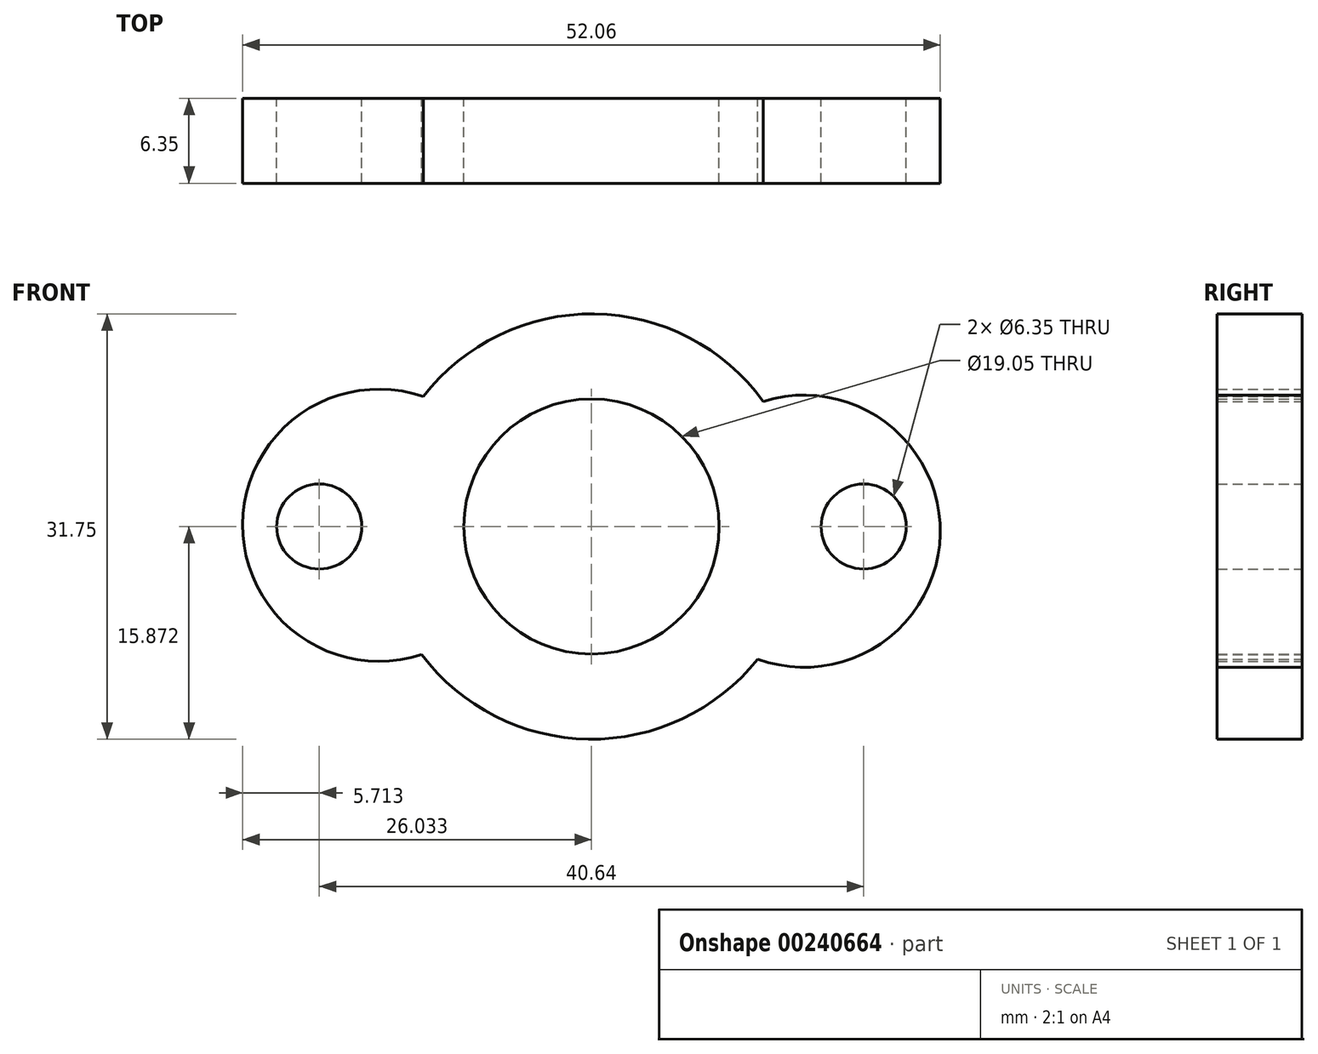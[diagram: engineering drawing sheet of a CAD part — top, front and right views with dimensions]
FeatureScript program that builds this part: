
annotation { "Feature Type Name" : "Feature", "Feature Type Description" : "" }
export const myFeature = defineFeature(function(context is Context, id is Id, definition is map)
    precondition{}
    {
        {
            var Q0;
            Q0=qCreatedBy(makeId("Front.planeOp"),FACE);
            var sketch = newSketch(context, id + "F0", { "sketchPlane" : qUnion([Q0])});
            skCircle(sketch, "E0", {"center": v(-58.59, -37.7) * mm, "radius": 3.18 * mm});
            skCircle(sketch, "E1.0", {"center": v(-58.59, -37.7) * mm, "radius": 9.53 * mm});
            skCircle(sketch, "E2.0", {"center": v(-58.59, -37.7) * mm, "radius": 15.88 * mm});
            skArc(sketch, "E3", {"start": v(-46.18, -47.6) * mm, "mid": v(-32.56, -38.28) * mm, "end": v(-45.76, -28.36) * mm});
            skArc(sketch, "E4", {"start": v(-71.15, -28) * mm, "mid": v(-84.62, -37.55) * mm, "end": v(-71.27, -47.26) * mm});
            skLineSegment(sketch, "E5", {"start": v(-58.59, -37.7) * mm, "end": v(-78.9, -37.7) * mm});
            skLineSegment(sketch, "E6", {"start": v(-58.59, -37.7) * mm, "end": v(-38.27, -37.7) * mm});
            skCircle(sketch, "E7", {"center": v(-38.27, -37.7) * mm, "radius": 3.18 * mm});
            skCircle(sketch, "E8", {"center": v(-78.9, -37.7) * mm, "radius": 3.18 * mm});
            skCircle(sketch, "E9", {"center": v(31.02, -26.4) * mm, "radius": 6.35 * mm});
            skCircle(sketch, "E10.0", {"center": v(31.02, -26.4) * mm, "radius": 12.7 * mm});
            skCircle(sketch, "E11.0", {"center": v(31.02, -26.4) * mm, "radius": 19.05 * mm});
            skArc(sketch, "E12", {"start": v(45.93, -38.26) * mm, "mid": v(62.77, -26.15) * mm, "end": v(45.74, -14.31) * mm});
            skArc(sketch, "E13", {"start": v(16.3, -14.31) * mm, "mid": v(-0.73, -26.15) * mm, "end": v(16.11, -38.26) * mm});
            skPoint(sketch, "E14.endSnap0", {"position": v(-0.73, -26.15) * mm});
            skPoint(sketch, "E15.trimOffspring.end.orphan", {"position": v(62.77, -26.15) * mm});
            skSolve(sketch);
        }
        {
            var Q0;
            {var subQ0=sQuery(id+"F0.wireOp",EDGE,"E4");Q0=makeQuery(id+"F0.imprint","IMPRINT",FACE,{"disambiguationData":[TD([[makeQuery(id+"F0.imprint","IMPRINT",EDGE,{"derivedFrom":subQ0}),1.0]])]});}
            var Q1;
            {var subQ2=sQuery(id+"F0.wireOp",EDGE,"E5");var subQ6=sQuery(id+"F0.wireOp",EDGE,"E1.0");var subQ9=makeQuery(id+"F0.imprint","INTERSECT",VERTEX,{"derivedFrom":[subQ6,subQ2]});Q1=makeQuery(id+"F0.imprint","IMPRINT",FACE,{"disambiguationData":[TD([[makeQuery(id+"F0.imprint","IMPRINT",EDGE,{"disambiguationData":[TD([[subQ9,1.0]])],"derivedFrom":subQ6}),-1.0]])]});}
            var Q2;
            {var subQ5=sQuery(id+"F0.wireOp",EDGE,"E5");var subQ7=sQuery(id+"F0.wireOp",EDGE,"E1.0");var subQ8=makeQuery(id+"F0.imprint","INTERSECT",VERTEX,{"derivedFrom":[subQ7,subQ5]});Q2=makeQuery(id+"F0.imprint","IMPRINT",FACE,{"disambiguationData":[TD([[makeQuery(id+"F0.imprint","IMPRINT",EDGE,{"disambiguationData":[TD([[subQ8,-1.0]])],"derivedFrom":subQ7}),-1.0]])]});}
            var Q3;
            {var subQ0=sQuery(id+"F0.wireOp",EDGE,"E3");Q3=makeQuery(id+"F0.imprint","IMPRINT",FACE,{"disambiguationData":[TD([[makeQuery(id+"F0.imprint","IMPRINT",EDGE,{"derivedFrom":subQ0}),1.0]])]});}
            extrude(context, id + "F1", {"entities" : qUnion([Q0, Q1, Q2, Q3]), "depth" : 6.35 * mm});
        }
    });
